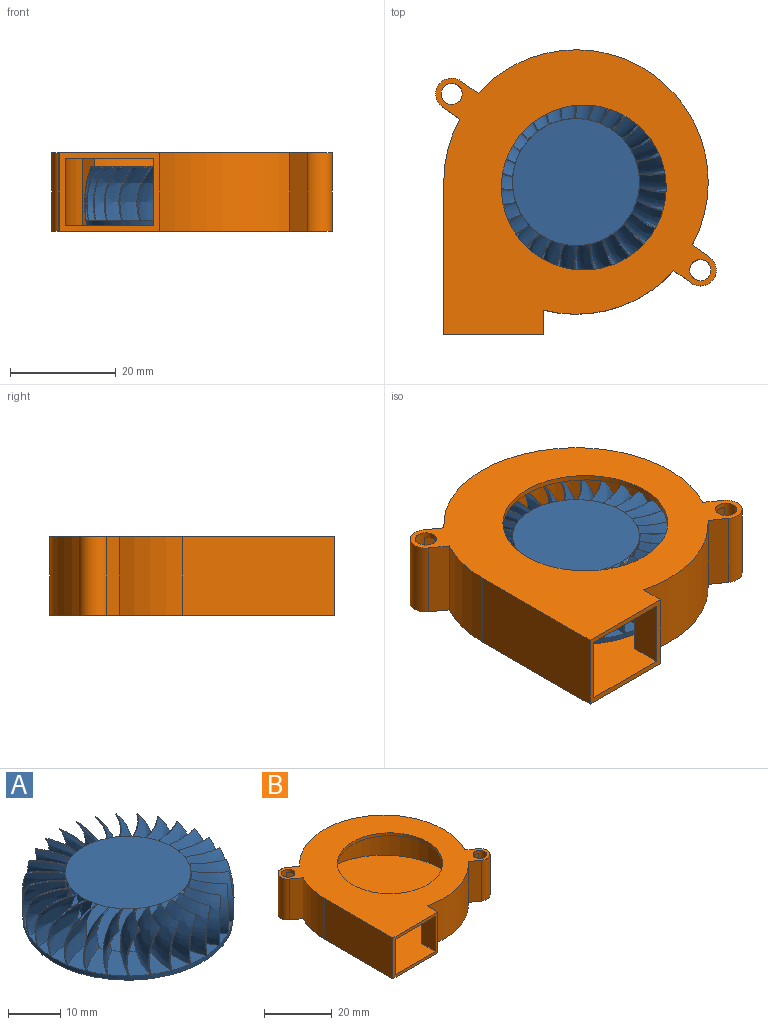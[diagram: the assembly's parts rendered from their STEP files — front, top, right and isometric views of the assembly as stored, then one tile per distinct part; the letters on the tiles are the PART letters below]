
ASSEMBLY  parts=2 mates=1
PART A: 275 faces, bbox 88.8x88.6x59.1 mm
  f0: plane 8.28x4.32mm, normal (0,0,1), area 25.1mm2, adj f1,f271,f273,f274
  f1: offset ~10.4x8.6mm, area 89.1mm2, adj f0,f2,f266,f267,f268,f269,f270,f271
  f2: bspline ~6.56x0.74mm, area 1mm2, adj f1,f3,f266,f274
  f3: bspline ~10x8.2mm, area 86.9mm2, adj f2,f4,f267,f268,f269
  f4: plane 8.19x5.34mm, normal (0,0,1), area 25.1mm2, adj f3,f5,f271,f274
  f5: offset ~10.4x8.69mm, area 89.1mm2, adj f4,f6,f261,f262,f263,f264,f265,f271
  f6: bspline ~6.56x0.73mm, area 1mm2, adj f5,f7,f261,f274
  f7: bspline ~10x8.29mm, area 86.9mm2, adj f6,f8,f262,f263,f264
  f8: plane 8.2x6.7mm, normal (0,0,1), area 25.1mm2, adj f7,f9,f271,f274
  f9: offset ~10.4x8.41mm, area 89.1mm2, adj f8,f10,f256,f257,f258,f259,f260,f271
  f10: bspline ~6.56x0.68mm, area 1mm2, adj f9,f11,f256,f274
  f11: bspline ~10x8.01mm, area 86.9mm2, adj f10,f12,f257,f258,f259
  f12: plane 7.85x7.81mm, normal (0,0,1), area 25.1mm2, adj f11,f13,f271,f274
  f13: offset ~10.4x7.79mm, area 89.1mm2, adj f12,f14,f251,f252,f253,f254,f255,f271
  f14: bspline ~6.56x0.61mm, area 1mm2, adj f13,f15,f251,f274
  f15: bspline ~10x7.39mm, area 86.9mm2, adj f14,f16,f252,f253,f254
  f16: plane 8.57x7.16mm, normal (0,0,1), area 25.1mm2, adj f15,f17,f271,f274
  f17: offset ~10.4x8.14mm, area 89.1mm2, adj f16,f18,f246,f247,f248,f249,f250,f271
  f18: bspline ~6.56x0.54mm, area 1mm2, adj f17,f19,f246,f274
  f19: bspline ~10x7.74mm, area 86.9mm2, adj f18,f20,f247,f248,f249
  f20: plane 8.97x6.16mm, normal (0,0,1), area 25.1mm2, adj f19,f21,f271,f274
  f21: offset ~10.4x8.34mm, area 89.1mm2, adj f20,f22,f241,f242,f243,f244,f245,f271
  f22: bspline ~6.56x0.63mm, area 1mm2, adj f21,f23,f241,f274
  f23: bspline ~10x7.94mm, area 86.9mm2, adj f22,f24,f242,f243,f244
  f24: plane 8.97x4.89mm, normal (0,0,1), area 25.1mm2, adj f23,f25,f271,f274
  f25: offset ~10.4x8.65mm, area 89.1mm2, adj f24,f26,f236,f237,f238,f239,f240,f271
  f26: bspline ~6.56x0.7mm, area 1mm2, adj f25,f27,f236,f274
  f27: bspline ~10x8.25mm, area 86.9mm2, adj f26,f28,f237,f238,f239
  f28: plane 8.58x4.01mm, normal (0,0,1), area 25.1mm2, adj f27,f29,f271,f274
  f29: offset ~10.4x8.71mm, area 89.1mm2, adj f28,f30,f231,f232,f233,f234,f235,f271
  f30: bspline ~6.56x0.74mm, area 1mm2, adj f29,f31,f231,f274
  f31: bspline ~10x8.31mm, area 86.9mm2, adj f30,f32,f232,f233,f234
  f32: plane 8.08x4.76mm, normal (0,0,1), area 25.1mm2, adj f31,f33,f271,f274
  f33: offset ~10.4x8.69mm, area 89.1mm2, adj f32,f34,f226,f227,f228,f229,f230,f271
  f34: bspline ~6.56x0.74mm, area 1mm2, adj f33,f35,f226,f274
  f35: bspline ~10x8.68mm, area 86.9mm2, adj f34,f36,f227,f228,f229
  f36: plane 8.24x6.03mm, normal (0,0,1), area 25.1mm2, adj f35,f37,f271,f274
  f37: offset ~10.4x8.6mm, area 89.1mm2, adj f36,f38,f221,f222,f223,f224,f225,f271
  f38: bspline ~6.56x0.71mm, area 1mm2, adj f37,f39,f221,f274
  f39: bspline ~10x8.7mm, area 86.9mm2, adj f38,f40,f222,f223,f224
  f40: plane 8.07x7.29mm, normal (0,0,1), area 25.1mm2, adj f39,f41,f271,f274
  f41: offset ~10.4x8.14mm, area 89.1mm2, adj f40,f42,f216,f217,f218,f219,f220,f271
  f42: bspline ~6.56x0.65mm, area 1mm2, adj f41,f43,f216,f274
  f43: bspline ~10x7.74mm, area 86.9mm2, adj f42,f44,f217,f218,f219
  f44: plane 8.24x7.55mm, normal (0,0,1), area 25.1mm2, adj f43,f45,f271,f274
  f45: offset ~10.4x7.91mm, area 89.1mm2, adj f44,f46,f211,f212,f213,f214,f215,f271
  f46: bspline ~6.56x0.56mm, area 1mm2, adj f45,f47,f211,f274
  f47: bspline ~10x7.51mm, area 86.9mm2, adj f46,f48,f212,f213,f214
  f48: plane 8.82x6.7mm, normal (0,0,1), area 25.1mm2, adj f47,f49,f271,f274
  f49: offset ~10.4x8.28mm, area 89.1mm2, adj f48,f50,f206,f207,f208,f209,f210,f271
  f50: bspline ~6.56x0.59mm, area 1mm2, adj f49,f51,f206,f274
  f51: bspline ~10x7.88mm, area 86.9mm2, adj f50,f52,f207,f208,f209
  f52: plane 9.02x5.55mm, normal (0,0,1), area 25.1mm2, adj f51,f53,f271,f274
  f53: offset ~10.4x8.81mm, area 89.1mm2, adj f52,f54,f201,f202,f203,f204,f205,f271
  f54: bspline ~6.56x0.67mm, area 1mm2, adj f53,f55,f201,f274
  f55: bspline ~10x8.08mm, area 86.9mm2, adj f54,f56,f202,f203,f204
  f56: plane 8.82x4.17mm, normal (0,0,1), area 25.1mm2, adj f55,f57,f271,f274
  f57: offset ~10.4x8.72mm, area 89.1mm2, adj f56,f58,f196,f197,f198,f199,f200,f271
  f58: bspline ~6.56x0.72mm, area 1mm2, adj f57,f59,f196,f274
  f59: bspline ~10x8.32mm, area 86.9mm2, adj f58,f60,f197,f198,f199
  f60: plane 8.28x4.32mm, normal (0,0,1), area 25.1mm2, adj f59,f61,f271,f274
  f61: offset ~10.4x8.6mm, area 89.1mm2, adj f60,f62,f191,f192,f193,f194,f195,f271
  f62: bspline ~6.56x0.74mm, area 1mm2, adj f61,f63,f191,f274
  f63: bspline ~10x8.2mm, area 86.9mm2, adj f62,f64,f192,f193,f194
  f64: plane 8.19x5.34mm, normal (0,0,1), area 25.1mm2, adj f63,f65,f271,f274
  f65: offset ~10.4x8.69mm, area 89.1mm2, adj f64,f66,f186,f187,f188,f189,f190,f271
  f66: bspline ~6.56x0.73mm, area 1mm2, adj f65,f67,f186,f274
  f67: bspline ~10x8.29mm, area 86.9mm2, adj f66,f68,f187,f188,f189
  f68: plane 8.2x6.7mm, normal (0,0,1), area 25.1mm2, adj f67,f69,f271,f274
  f69: offset ~10.4x8.41mm, area 89.1mm2, adj f68,f70,f181,f182,f183,f184,f185,f271
  f70: bspline ~6.56x0.68mm, area 1mm2, adj f69,f71,f181,f274
  f71: bspline ~10x8.01mm, area 86.9mm2, adj f70,f72,f182,f183,f184
  f72: plane 7.85x7.81mm, normal (0,0,1), area 25.1mm2, adj f71,f73,f271,f274
  f73: offset ~10.4x7.79mm, area 89.1mm2, adj f72,f74,f176,f177,f178,f179,f180,f271
  f74: bspline ~6.56x0.61mm, area 1mm2, adj f73,f75,f176,f274
  f75: bspline ~10x7.39mm, area 86.9mm2, adj f74,f76,f177,f178,f179
  f76: plane 8.57x7.16mm, normal (0,0,1), area 25.1mm2, adj f75,f77,f271,f274
  f77: offset ~10.4x8.14mm, area 89.1mm2, adj f76,f78,f171,f172,f173,f174,f175,f271
  f78: bspline ~6.56x0.54mm, area 1mm2, adj f77,f79,f171,f274
  f79: bspline ~10x7.74mm, area 86.9mm2, adj f78,f80,f172,f173,f174
  f80: plane 8.97x6.16mm, normal (0,0,1), area 25.1mm2, adj f79,f81,f271,f274
  f81: offset ~10.4x8.34mm, area 89.1mm2, adj f80,f82,f166,f167,f168,f169,f170,f271
  f82: bspline ~6.56x0.63mm, area 1mm2, adj f81,f83,f166,f274
  f83: bspline ~10x7.94mm, area 86.9mm2, adj f82,f84,f167,f168,f169
  f84: plane 8.97x4.89mm, normal (0,0,1), area 25.1mm2, adj f83,f85,f271,f274
  f85: offset ~10.4x8.65mm, area 89.1mm2, adj f84,f86,f161,f162,f163,f164,f165,f271
  f86: bspline ~6.56x0.7mm, area 1mm2, adj f85,f87,f161,f274
  f87: bspline ~10x8.25mm, area 86.9mm2, adj f86,f88,f162,f163,f164
  f88: plane 8.58x4.01mm, normal (0,0,1), area 25.1mm2, adj f87,f89,f271,f274
  f89: offset ~10.4x8.71mm, area 89.1mm2, adj f88,f90,f156,f157,f158,f159,f160,f271
  f90: bspline ~6.56x0.74mm, area 1mm2, adj f89,f91,f156,f274
  f91: bspline ~10x8.31mm, area 86.9mm2, adj f90,f92,f157,f158,f159
  f92: plane 8.08x4.76mm, normal (0,0,1), area 25.1mm2, adj f91,f93,f95,f271,f274
  f93: cylinder r=12mm len=10mm, axis (0,0,-1), area 0.2mm2, adj f92,f94,f95,f274
  f94: plane 72x72mm, normal (0,0,1), area 452.4mm2, adj f93
  f95: offset ~10.4x8.69mm, area 89.1mm2, adj f92,f93,f96,f151,f152,f153,f154,f155
  f96: bspline ~6.56x0.74mm, area 1mm2, adj f95,f97,f151,f274
  f97: bspline ~10x8.68mm, area 86.9mm2, adj f96,f98,f152,f153,f154
  f98: plane 8.24x6.03mm, normal (0,0,1), area 25.1mm2, adj f97,f99,f271,f274
  f99: offset ~10.4x8.6mm, area 89.1mm2, adj f98,f100,f146,f147,f148,f149,f150,f271
  f100: bspline ~6.56x0.71mm, area 1mm2, adj f99,f101,f146,f274
  f101: bspline ~10x8.7mm, area 86.9mm2, adj f100,f102,f147,f148,f149
  f102: plane 8.07x7.29mm, normal (0,0,1), area 25.1mm2, adj f101,f103,f271,f274
  f103: offset ~10.4x8.14mm, area 89.1mm2, adj f102,f104,f141,f142,f143,f144,f145,f271
  f104: bspline ~6.56x0.65mm, area 1mm2, adj f103,f105,f141,f274
  f105: bspline ~10x7.74mm, area 86.9mm2, adj f104,f106,f142,f143,f144
  f106: plane 8.24x7.55mm, normal (0,0,1), area 25.1mm2, adj f105,f107,f271,f274
  f107: offset ~10.4x7.91mm, area 89.1mm2, adj f106,f108,f136,f137,f138,f139,f140,f271
  f108: bspline ~6.56x0.56mm, area 1mm2, adj f107,f109,f136,f274
  f109: bspline ~10x7.51mm, area 86.9mm2, adj f108,f110,f137,f138,f139
  f110: plane 8.82x6.7mm, normal (0,0,1), area 25.1mm2, adj f109,f111,f271,f274
  f111: offset ~10.4x8.28mm, area 89.1mm2, adj f110,f112,f131,f132,f133,f134,f135,f271
  f112: bspline ~6.56x0.59mm, area 1mm2, adj f111,f113,f131,f274
  f113: bspline ~10x7.88mm, area 86.9mm2, adj f112,f114,f132,f133,f134
  f114: plane 9.02x5.55mm, normal (0,0,1), area 25.1mm2, adj f113,f115,f271,f274
  f115: offset ~10.4x8.81mm, area 89.1mm2, adj f114,f116,f126,f127,f128,f129,f130,f271
  f116: bspline ~6.56x0.67mm, area 1mm2, adj f115,f117,f126,f274
  f117: bspline ~10x8.08mm, area 86.9mm2, adj f116,f118,f127,f128,f129
  f118: plane 56.81x52.15mm, normal (0,0,1), area 25.1mm2, adj f117,f119,f271,f274
  f119: offset ~10.4x8.72mm, area 89.1mm2, adj f118,f120,f121,f122,f123,f124,f125,f271
  f120: bspline ~6.56x0.72mm, area 1mm2, adj f119,f121,f273,f274
  f121: cylinder r=12mm len=3.05mm, axis (0,0,-1), area 0.1mm2, adj f119,f120,f122
  f122: bspline ~5.71x2.82mm, area 0.7mm2, adj f119,f121,f123,f273
  f123: cone r=14.72mm half-angle=46.3deg, axis (0,0,1), area 1.4mm2, adj f119,f122,f124,f273
  f124: bspline ~10.2x2.86mm, area 2.2mm2, adj f119,f123,f125,f273
  f125: cone r=16.9mm half-angle=70.9deg, axis (0,0,-1), area 0mm2, adj f119,f124,f271
  f126: cylinder r=12mm len=3.05mm, axis (0,0,-1), area 0.1mm2, adj f115,f116,f127
  f127: bspline ~5.71x2.64mm, area 0.7mm2, adj f115,f117,f126,f128
  f128: cone r=14.72mm half-angle=46.3deg, axis (0,0,1), area 1.4mm2, adj f115,f117,f127,f129
  f129: bspline ~10.2x2.96mm, area 2.2mm2, adj f115,f117,f128,f130
  f130: cone r=16.9mm half-angle=70.9deg, axis (0,0,-1), area 0mm2, adj f115,f129,f271
  f131: cylinder r=12mm len=3.05mm, axis (0,0,-1), area 0.1mm2, adj f111,f112,f132
  f132: bspline ~3.71x1.91mm, area 0.7mm2, adj f111,f113,f131,f133
  f133: cone r=14.72mm half-angle=46.3deg, axis (0,0,1), area 1.4mm2, adj f111,f113,f132,f134
  f134: bspline ~10.2x2.93mm, area 2.2mm2, adj f111,f113,f133,f135
  f135: cone r=16.9mm half-angle=70.9deg, axis (0,0,-1), area 0mm2, adj f111,f134,f271
  f136: cylinder r=12mm len=3.05mm, axis (0,0,-1), area 0.1mm2, adj f107,f108,f137
  f137: bspline ~3.71x1.77mm, area 0.7mm2, adj f107,f109,f136,f138
  f138: cone r=14.72mm half-angle=46.3deg, axis (0,0,1), area 1.4mm2, adj f107,f109,f137,f139
  f139: bspline ~10.2x2.77mm, area 2.2mm2, adj f107,f109,f138,f140
  f140: cone r=16.9mm half-angle=70.9deg, axis (0,0,-1), area 0mm2, adj f107,f139,f271
  f141: cylinder r=12mm len=3.05mm, axis (0,0,-1), area 0.1mm2, adj f103,f104,f142
  f142: bspline ~3.71x2.06mm, area 0.7mm2, adj f103,f105,f141,f143
  f143: cone r=14.72mm half-angle=46.3deg, axis (0,0,1), area 1.4mm2, adj f103,f105,f142,f144
  f144: bspline ~10.2x2.5mm, area 2.2mm2, adj f103,f105,f143,f145
  f145: cone r=16.9mm half-angle=70.9deg, axis (0,0,-1), area 0mm2, adj f103,f144,f271
  f146: cylinder r=12mm len=3.05mm, axis (0,0,-1), area 0.1mm2, adj f99,f100,f147
  f147: bspline ~3.71x2.26mm, area 0.7mm2, adj f99,f101,f146,f148
  f148: cone r=14.72mm half-angle=46.3deg, axis (0,0,1), area 1.4mm2, adj f99,f101,f147,f149
  f149: bspline ~10.2x2.11mm, area 2.2mm2, adj f99,f101,f148,f150
  f150: cone r=16.9mm half-angle=70.9deg, axis (0,0,-1), area 0mm2, adj f99,f149,f271
  f151: cylinder r=12mm len=3.05mm, axis (0,0,-1), area 0.1mm2, adj f95,f96,f152
  f152: bspline ~5.71x2.88mm, area 0.7mm2, adj f95,f97,f151,f153
  f153: cone r=14.72mm half-angle=46.3deg, axis (0,0,1), area 1.4mm2, adj f95,f97,f152,f154
  f154: bspline ~10.2x2.47mm, area 2.2mm2, adj f95,f97,f153,f155
  f155: cone r=16.9mm half-angle=70.9deg, axis (0,0,-1), area 0mm2, adj f95,f154,f271
  f156: cylinder r=12mm len=3.05mm, axis (0,0,-1), area 0.1mm2, adj f89,f90,f157
  f157: bspline ~3.71x2.36mm, area 0.7mm2, adj f89,f91,f156,f158
  f158: cone r=14.72mm half-angle=46.3deg, axis (0,0,1), area 1.4mm2, adj f89,f91,f157,f159
  f159: bspline ~10.2x2.76mm, area 2.2mm2, adj f89,f91,f158,f160
  f160: cone r=16.9mm half-angle=70.9deg, axis (0,0,-1), area 0mm2, adj f89,f159,f271
  f161: cylinder r=12mm len=3.05mm, axis (0,0,-1), area 0.1mm2, adj f85,f86,f162
  f162: bspline ~3.71x2.25mm, area 0.7mm2, adj f85,f87,f161,f163
  f163: cone r=14.72mm half-angle=46.3deg, axis (0,0,1), area 1.4mm2, adj f85,f87,f162,f164
  f164: bspline ~10.2x2.92mm, area 2.2mm2, adj f85,f87,f163,f165
  f165: cone r=16.9mm half-angle=70.9deg, axis (0,0,-1), area 0mm2, adj f85,f164,f271
  f166: cylinder r=12mm len=3.05mm, axis (0,0,-1), area 0.1mm2, adj f81,f82,f167
  f167: bspline ~3.71x2.05mm, area 0.7mm2, adj f81,f83,f166,f168
  f168: cone r=14.72mm half-angle=46.3deg, axis (0,0,1), area 1.4mm2, adj f81,f83,f167,f169
  f169: bspline ~10.2x2.96mm, area 2.2mm2, adj f81,f83,f168,f170
  f170: cone r=16.9mm half-angle=70.9deg, axis (0,0,-1), area 0mm2, adj f81,f169,f271
  f171: cylinder r=12mm len=3.05mm, axis (0,0,-1), area 0.1mm2, adj f77,f78,f172
  f172: bspline ~3.71x1.76mm, area 0.7mm2, adj f77,f79,f171,f173
  f173: cone r=14.72mm half-angle=46.3deg, axis (0,0,1), area 1.4mm2, adj f77,f79,f172,f174
  f174: bspline ~10.2x2.87mm, area 2.2mm2, adj f77,f79,f173,f175
  f175: cone r=16.9mm half-angle=70.9deg, axis (0,0,-1), area 0mm2, adj f77,f174,f271
  f176: cylinder r=12mm len=3.05mm, axis (0,0,-1), area 0.1mm2, adj f73,f74,f177
  f177: bspline ~3.71x1.93mm, area 0.7mm2, adj f73,f75,f176,f178
  f178: cone r=14.72mm half-angle=46.3deg, axis (0,0,1), area 1.4mm2, adj f73,f75,f177,f179
  f179: bspline ~10.2x2.65mm, area 2.2mm2, adj f73,f75,f178,f180
  f180: cone r=16.9mm half-angle=70.9deg, axis (0,0,-1), area 0mm2, adj f73,f179,f271
  f181: cylinder r=12mm len=3.05mm, axis (0,0,-1), area 0.1mm2, adj f69,f70,f182
  f182: bspline ~5.71x2.65mm, area 0.7mm2, adj f69,f71,f181,f183
  f183: cone r=14.72mm half-angle=46.3deg, axis (0,0,1), area 1.4mm2, adj f69,f71,f182,f184
  f184: bspline ~10.2x2.31mm, area 2.2mm2, adj f69,f71,f183,f185
  f185: cone r=16.9mm half-angle=70.9deg, axis (0,0,-1), area 0mm2, adj f69,f184,f271
  f186: cylinder r=12mm len=3.05mm, axis (0,0,-1), area 0.1mm2, adj f65,f66,f187
  f187: bspline ~3.71x2.32mm, area 0.7mm2, adj f65,f67,f186,f188
  f188: cone r=14.72mm half-angle=46.3deg, axis (0,0,1), area 1.4mm2, adj f65,f67,f187,f189
  f189: bspline ~10.2x2.29mm, area 2.2mm2, adj f65,f67,f188,f190
  f190: cone r=16.9mm half-angle=70.9deg, axis (0,0,-1), area 0mm2, adj f65,f189,f271
  f191: cylinder r=12mm len=3.05mm, axis (0,0,-1), area 0.1mm2, adj f61,f62,f192
  f192: bspline ~3.71x2.37mm, area 0.7mm2, adj f61,f63,f191,f193
  f193: cone r=14.72mm half-angle=46.3deg, axis (0,0,1), area 1.4mm2, adj f61,f63,f192,f194
  f194: bspline ~10.2x2.63mm, area 2.2mm2, adj f61,f63,f193,f195
  f195: cone r=16.9mm half-angle=70.9deg, axis (0,0,-1), area 0mm2, adj f61,f194,f271
  f196: cylinder r=12mm len=3.05mm, axis (0,0,-1), area 0.1mm2, adj f57,f58,f197
  f197: bspline ~5.71x2.82mm, area 0.7mm2, adj f57,f59,f196,f198
  f198: cone r=14.72mm half-angle=46.3deg, axis (0,0,1), area 1.4mm2, adj f57,f59,f197,f199
  f199: bspline ~10.2x2.86mm, area 2.2mm2, adj f57,f59,f198,f200
  f200: cone r=16.9mm half-angle=70.9deg, axis (0,0,-1), area 0mm2, adj f57,f199,f271
  f201: cylinder r=12mm len=3.05mm, axis (0,0,-1), area 0.1mm2, adj f53,f54,f202
  f202: bspline ~5.71x2.64mm, area 0.7mm2, adj f53,f55,f201,f203
  f203: cone r=14.72mm half-angle=46.3deg, axis (0,0,1), area 1.4mm2, adj f53,f55,f202,f204
  f204: bspline ~10.2x2.96mm, area 2.2mm2, adj f53,f55,f203,f205
  f205: cone r=16.9mm half-angle=70.9deg, axis (0,0,-1), area 0mm2, adj f53,f204,f271
  f206: cylinder r=12mm len=3.05mm, axis (0,0,-1), area 0.1mm2, adj f49,f50,f207
  f207: bspline ~3.71x1.91mm, area 0.7mm2, adj f49,f51,f206,f208
  f208: cone r=14.72mm half-angle=46.3deg, axis (0,0,1), area 1.4mm2, adj f49,f51,f207,f209
  f209: bspline ~10.2x2.93mm, area 2.2mm2, adj f49,f51,f208,f210
  f210: cone r=16.9mm half-angle=70.9deg, axis (0,0,-1), area 0mm2, adj f49,f209,f271
  f211: cylinder r=12mm len=3.05mm, axis (0,0,-1), area 0.1mm2, adj f45,f46,f212
  f212: bspline ~3.71x1.77mm, area 0.7mm2, adj f45,f47,f211,f213
  f213: cone r=14.72mm half-angle=46.3deg, axis (0,0,1), area 1.4mm2, adj f45,f47,f212,f214
  f214: bspline ~10.2x2.77mm, area 2.2mm2, adj f45,f47,f213,f215
  f215: cone r=16.9mm half-angle=70.9deg, axis (0,0,-1), area 0mm2, adj f45,f214,f271
  f216: cylinder r=12mm len=3.05mm, axis (0,0,-1), area 0.1mm2, adj f41,f42,f217
  f217: bspline ~3.71x2.06mm, area 0.7mm2, adj f41,f43,f216,f218
  f218: cone r=14.72mm half-angle=46.3deg, axis (0,0,1), area 1.4mm2, adj f41,f43,f217,f219
  f219: bspline ~10.2x2.5mm, area 2.2mm2, adj f41,f43,f218,f220
  f220: cone r=16.9mm half-angle=70.9deg, axis (0,0,-1), area 0mm2, adj f41,f219,f271
  f221: cylinder r=12mm len=3.05mm, axis (0,0,-1), area 0.1mm2, adj f37,f38,f222
  f222: bspline ~3.71x2.26mm, area 0.7mm2, adj f37,f39,f221,f223
  f223: cone r=14.72mm half-angle=46.3deg, axis (0,0,1), area 1.4mm2, adj f37,f39,f222,f224
  f224: bspline ~10.2x2.11mm, area 2.2mm2, adj f37,f39,f223,f225
  f225: cone r=16.9mm half-angle=70.9deg, axis (0,0,-1), area 0mm2, adj f37,f224,f271
  f226: cylinder r=12mm len=3.05mm, axis (0,0,-1), area 0.1mm2, adj f33,f34,f227
  f227: bspline ~5.71x2.88mm, area 0.7mm2, adj f33,f35,f226,f228
  f228: cone r=14.72mm half-angle=46.3deg, axis (0,0,1), area 1.4mm2, adj f33,f35,f227,f229
  f229: bspline ~10.2x2.47mm, area 2.2mm2, adj f33,f35,f228,f230
  f230: cone r=16.9mm half-angle=70.9deg, axis (0,0,-1), area 0mm2, adj f33,f229,f271
  f231: cylinder r=12mm len=3.05mm, axis (0,0,-1), area 0.1mm2, adj f29,f30,f232
  f232: bspline ~3.71x2.36mm, area 0.7mm2, adj f29,f31,f231,f233
  f233: cone r=14.72mm half-angle=46.3deg, axis (0,0,1), area 1.4mm2, adj f29,f31,f232,f234
  f234: bspline ~10.2x2.76mm, area 2.2mm2, adj f29,f31,f233,f235
  f235: cone r=16.9mm half-angle=70.9deg, axis (0,0,-1), area 0mm2, adj f29,f234,f271
  f236: cylinder r=12mm len=3.05mm, axis (0,0,-1), area 0.1mm2, adj f25,f26,f237
  f237: bspline ~3.71x2.25mm, area 0.7mm2, adj f25,f27,f236,f238
  f238: cone r=14.72mm half-angle=46.3deg, axis (0,0,1), area 1.4mm2, adj f25,f27,f237,f239
  f239: bspline ~10.2x2.92mm, area 2.2mm2, adj f25,f27,f238,f240
  f240: cone r=16.9mm half-angle=70.9deg, axis (0,0,-1), area 0mm2, adj f25,f239,f271
  f241: cylinder r=12mm len=3.05mm, axis (0,0,-1), area 0.1mm2, adj f21,f22,f242
  f242: bspline ~3.71x2.05mm, area 0.7mm2, adj f21,f23,f241,f243
  f243: cone r=14.72mm half-angle=46.3deg, axis (0,0,1), area 1.4mm2, adj f21,f23,f242,f244
  f244: bspline ~10.2x2.96mm, area 2.2mm2, adj f21,f23,f243,f245
  f245: cone r=16.9mm half-angle=70.9deg, axis (0,0,-1), area 0mm2, adj f21,f244,f271
  f246: cylinder r=12mm len=3.05mm, axis (0,0,-1), area 0.1mm2, adj f17,f18,f247
  f247: bspline ~3.71x1.76mm, area 0.7mm2, adj f17,f19,f246,f248
  f248: cone r=14.72mm half-angle=46.3deg, axis (0,0,1), area 1.4mm2, adj f17,f19,f247,f249
  f249: bspline ~10.2x2.87mm, area 2.2mm2, adj f17,f19,f248,f250
  f250: cone r=16.9mm half-angle=70.9deg, axis (0,0,-1), area 0mm2, adj f17,f249,f271
  f251: cylinder r=12mm len=3.05mm, axis (0,0,-1), area 0.1mm2, adj f13,f14,f252
  f252: bspline ~3.71x1.93mm, area 0.7mm2, adj f13,f15,f251,f253
  f253: cone r=14.72mm half-angle=46.3deg, axis (0,0,1), area 1.4mm2, adj f13,f15,f252,f254
  f254: bspline ~10.2x2.65mm, area 2.2mm2, adj f13,f15,f253,f255
  f255: cone r=16.9mm half-angle=70.9deg, axis (0,0,-1), area 0mm2, adj f13,f254,f271
  f256: cylinder r=12mm len=3.05mm, axis (0,0,-1), area 0.1mm2, adj f9,f10,f257
  f257: bspline ~5.71x2.65mm, area 0.7mm2, adj f9,f11,f256,f258
  f258: cone r=14.72mm half-angle=46.3deg, axis (0,0,1), area 1.4mm2, adj f9,f11,f257,f259
  f259: bspline ~10.2x2.31mm, area 2.2mm2, adj f9,f11,f258,f260
  f260: cone r=16.9mm half-angle=70.9deg, axis (0,0,-1), area 0mm2, adj f9,f259,f271
  f261: cylinder r=12mm len=3.05mm, axis (0,0,-1), area 0.1mm2, adj f5,f6,f262
  f262: bspline ~3.71x2.32mm, area 0.7mm2, adj f5,f7,f261,f263
  f263: cone r=14.72mm half-angle=46.3deg, axis (0,0,1), area 1.4mm2, adj f5,f7,f262,f264
  f264: bspline ~10.2x2.29mm, area 2.2mm2, adj f5,f7,f263,f265
  f265: cone r=16.9mm half-angle=70.9deg, axis (0,0,-1), area 0mm2, adj f5,f264,f271
  f266: cylinder r=12mm len=3.05mm, axis (0,0,-1), area 0.1mm2, adj f1,f2,f267
  f267: bspline ~3.71x2.37mm, area 0.7mm2, adj f1,f3,f266,f268
  f268: cone r=14.72mm half-angle=46.3deg, axis (0,0,1), area 1.4mm2, adj f1,f3,f267,f269
  f269: bspline ~10.2x2.63mm, area 2.2mm2, adj f1,f3,f268,f270
  f270: cone r=16.9mm half-angle=70.9deg, axis (0,0,-1), area 0mm2, adj f1,f269,f271
  f271: cylinder r=20mm len=40mm, axis (0,0,-1), area 125.4mm2, adj f0,f1,f4,f5,f8,f9,f12,f13
  f272: plane 40x40mm, normal (0,0,-1), area 1256.6mm2, adj f271
  f273: bspline ~10x8.32mm, area 86.9mm2, adj f0,f120,f122,f123,f124
  f274: cylinder r=12mm len=24mm, axis (0,0,-1), area 21.4mm2, adj f0,f1,f2,f4,f5,f6,f8,f9
PART B: 28 faces, bbox 53x53.8x14.8 mm
  f0: plane 28.75x12.8mm, normal (1,0,0), area 368mm2, adj f1,f12,f25,f26
  f1: cylinder r=24mm len=12.8mm, axis (0,0,-1), area 163.7mm2, adj f0,f2,f25,f26
  f2: plane 12.8x3.98mm, normal (0.58,0.82,0), area 62.5mm2, adj f1,f3,f25,f26
  f3: cylinder r=2mm len=14.8mm, axis (0,0,-1), area 105.6mm2, adj f2,f4,f23,f24,f25,f26
  f4: plane 12.8x3.98mm, normal (-0.58,-0.82,0), area 62.5mm2, adj f3,f5,f25,f26
  f5: cylinder r=24mm len=42.36mm, axis (0,0,-1), area 913.8mm2, adj f4,f6,f25,f26
  f6: plane 12.8x3.98mm, normal (-0.58,-0.82,0), area 62.5mm2, adj f5,f7,f25,f26
  f7: cylinder r=2mm len=14.8mm, axis (0,0,-1), area 105.6mm2, adj f6,f8,f23,f24,f25,f26
  f8: plane 12.8x3.98mm, normal (0.58,0.82,0), area 62.5mm2, adj f7,f9,f25,f26
  f9: cylinder r=24mm len=25.56mm, axis (0,0,-1), area 361.2mm2, adj f8,f10,f25,f26
  f10: plane 12.8x5.86mm, normal (-1,0,0), area 75mm2, adj f9,f12,f25,f26
  f11: plane 28.75x14.8mm, normal (-1,0,0), area 425.5mm2, adj f12,f22,f23,f24
  f12: plane 18.8x14.8mm, normal (0,-1,0), area 63.2mm2, adj f0,f10,f11,f13,f23,f24,f25,f26
  f13: plane 14.8x4.53mm, normal (1,0,0), area 67.1mm2, adj f12,f14,f23,f24
  f14: cylinder r=25mm len=24.72mm, axis (0,0,-1), area 401.4mm2, adj f13,f15,f23,f24
  f15: plane 14.8x3.25mm, normal (-0.58,-0.82,0), area 58.9mm2, adj f14,f16,f23,f24
  f16: cylinder r=3mm len=14.8mm, axis (0,0,-1), area 139.5mm2, adj f15,f17,f23,f24
  f17: plane 14.8x3.25mm, normal (0.58,0.82,0), area 58.9mm2, adj f16,f18,f23,f24
  f18: cylinder r=25mm len=43.52mm, axis (0,0,-1), area 1073.4mm2, adj f17,f19,f23,f24
  f19: plane 14.8x3.25mm, normal (0.58,0.82,0), area 58.9mm2, adj f18,f20,f23,f24
  f20: cylinder r=3mm len=14.8mm, axis (0,0,-1), area 139.5mm2, adj f19,f21,f23,f24
  f21: plane 14.8x3.25mm, normal (-0.58,-0.82,0), area 58.9mm2, adj f20,f22,f23,f24
  f22: cylinder r=25mm len=14.8mm, axis (0,0,-1), area 183.6mm2, adj f11,f21,f23,f24
  f23: plane 53.75x53mm, normal (0,0,1), area 1451.5mm2, adj f3,f7,f11,f12,f13,f14,f15,f16
  f24: plane 53.75x53mm, normal (0,0,-1), area 2216mm2, adj f3,f7,f11,f12,f13,f14,f15,f16
  f25: plane 52.75x49.31mm, normal (0,0,1), area 2036.4mm2, adj f0,f1,f2,f3,f4,f5,f6,f7
  f26: plane 52.75x49.31mm, normal (0,0,-1), area 1271.9mm2, adj f0,f1,f2,f3,f4,f5,f6,f7
  f27: cylinder r=15.6mm len=31.2mm, axis (0,0,1), area 98mm2, adj f23,f26
PLACE A rot(axis=(0,0,-1),152.9deg) t=(0,0,1)mm
PLACE B at identity
MATE revolute A.f271 <-> B.f9  axis (0,0,-1) through (0,0,1)mm
